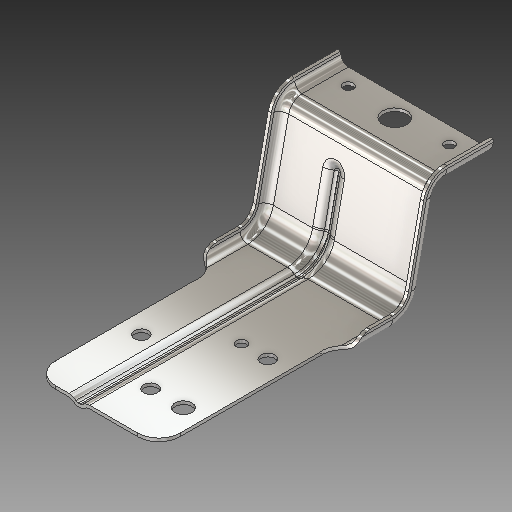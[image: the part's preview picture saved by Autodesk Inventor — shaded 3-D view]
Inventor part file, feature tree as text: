
AUTODESK INVENTOR PART (.ipt)
format: ipt  version: 2019 (Build 230136000, 136)  size: 616,448 bytes
history: native  units: in
note: dims shown in document units (in); Inventor stores cm internally (conversion verified against a paired STEP export)
features: sketch x5, other x3, plane x1
ambient origin geometry x8: Origin, YZ Plane, XZ Plane, XY Plane, X Axis, Y Axis, Z Axis, Center Point
bodies: Solid1 (feature_tree)
feature tree (9):
  other  "Power Mounting Bracket.ipt"
  other  "Solid1::Power Mounting Bracket.ipt"
  other  "TaggingFeature1"
  sketch  "Sketch2"  dims[d0=0.3937in]
  sketch  "Sketch3"
  sketch  "Sketch4"
  sketch  "Sketch5"
  sketch  "Sketch6"
  plane  "Work Plane1"
